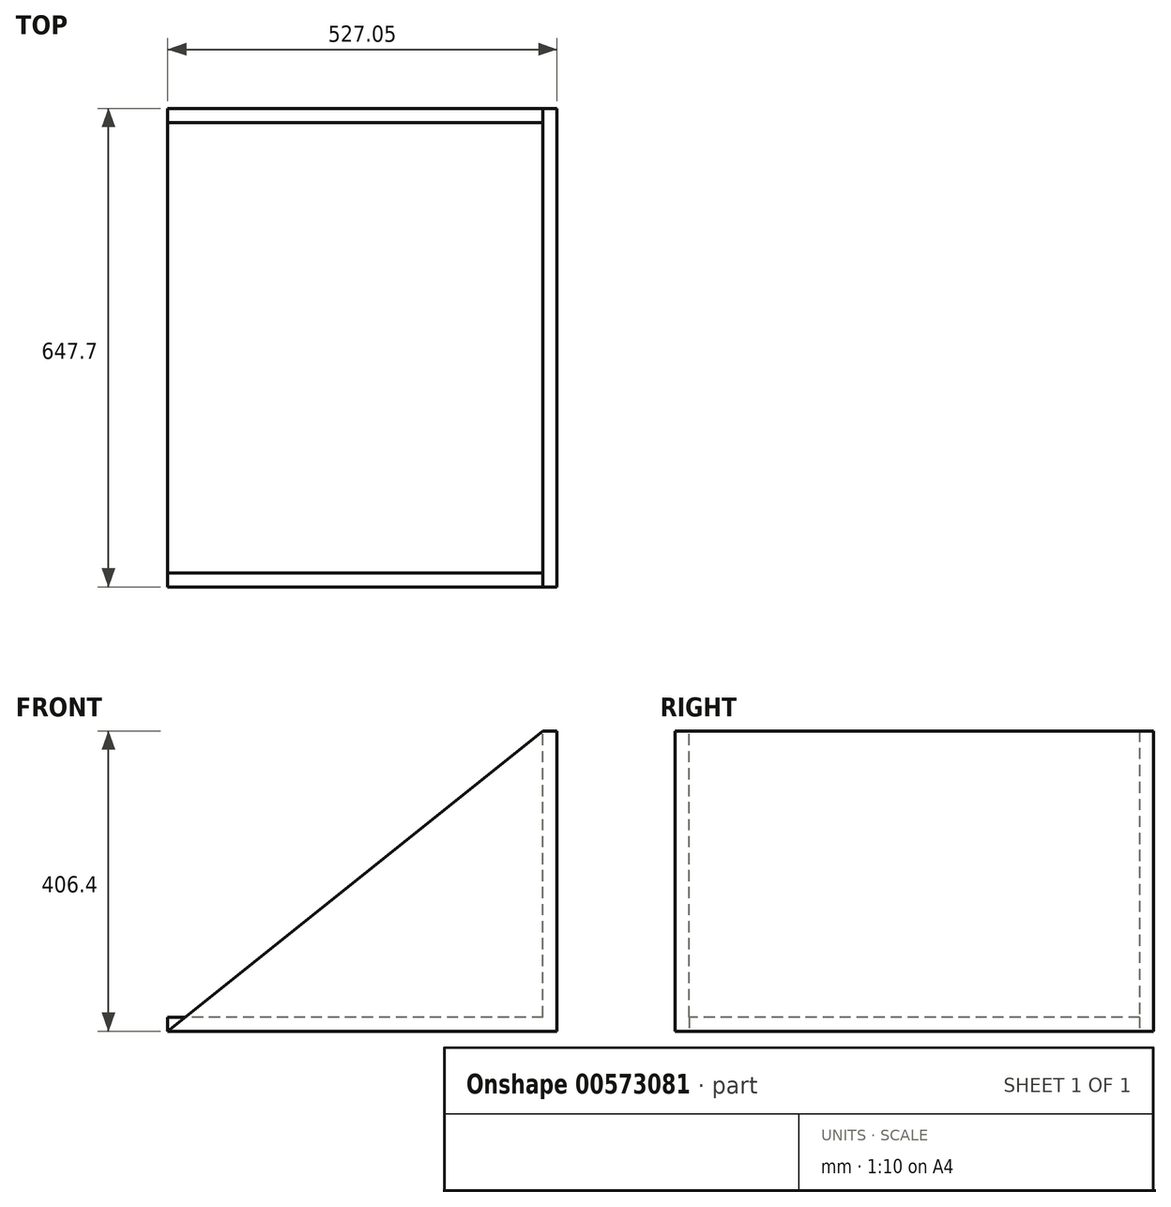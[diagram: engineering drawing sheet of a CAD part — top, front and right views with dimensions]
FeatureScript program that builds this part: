
annotation { "Feature Type Name" : "Feature", "Feature Type Description" : "" }
export const myFeature = defineFeature(function(context is Context, id is Id, definition is map)
    precondition{}
    {
        {
            var Q0;
            Q0=qCreatedBy(makeId("Top.planeOp"),FACE);
            var sketch = newSketch(context, id + "F0", { "sketchPlane" : qUnion([Q0])});
            skLineSegment(sketch, "E0.bottom", {"start": v(254, 304.8) * mm, "end": v(-254, 304.8) * mm});
            skLineSegment(sketch, "E0.top", {"start": v(254, -304.8) * mm, "end": v(-254, -304.8) * mm});
            skLineSegment(sketch, "E0.left", {"start": v(254, 304.8) * mm, "end": v(254, -304.8) * mm});
            skLineSegment(sketch, "E0.right", {"start": v(-254, 304.8) * mm, "end": v(-254, -304.8) * mm});
            skPoint(sketch, "E0.middle", {"position": v(0, 0) * mm});
            skSolve(sketch);
        }
        {
            var Q0;
            Q0=makeQuery(id+"F0.imprint","IMPRINT",FACE,{"disambiguationData":[TD([[makeQuery(id+"F0.imprint","IMPRINT",EDGE,{"derivedFrom":sQuery(id+"F0.wireOp",EDGE,"E0.bottom")}),1.0]])]});
            extrude(context, id + "F1", {"entities" : qUnion([Q0]), "depth" : 19.05 * mm, "offsetDistance" : 25.4 * mm});
        }
        {
            var Q0;
            Q0=makeQuery(id+"F1.opExtrude","SWEPT_FACE",FACE,{"disambiguationData":[OSD([sQuery(id+"F0.wireOp",EDGE,"E0.top")])]});
            var sketch = newSketch(context, id + "F2", { "sketchPlane" : qUnion([Q0])});
            skLineSegment(sketch, "E1.bottom", {"start": v(254, 0) * mm, "end": v(-254, 0) * mm});
            skLineSegment(sketch, "E1.left", {"start": v(254, 0) * mm, "end": v(254, 406.4) * mm});
            skLineSegment(sketch, "E2", {"start": v(254, 406.4) * mm, "end": v(-254, 0) * mm});
            skSolve(sketch);
        }
        {
            var Q0;
            {var subQ0=sQuery(id+"F2.wireOp",EDGE,"E1.left");var subQ3=sQuery(id+"F2.wireOp",EDGE,"E2");var subQ4=makeQuery(id+"F2.imprint","INTERSECT",VERTEX,{"derivedFrom":[subQ0,subQ3]});Q0=makeQuery(id+"F2.imprint","IMPRINT",FACE,{"disambiguationData":[TD([[makeQuery(id+"F2.imprint","IMPRINT",EDGE,{"disambiguationData":[TD([[subQ4,1.0]])],"derivedFrom":subQ0}),1.0]])]});}
            var Q1;
            {var subQ0=sQuery(id+"F2.wireOp",EDGE,"E1.bottom");Q1=makeQuery(id+"F2.imprint","IMPRINT",FACE,{"disambiguationData":[TD([[makeQuery(id+"F2.imprint","IMPRINT",EDGE,{"derivedFrom":subQ0}),-1.0]])]});}
            extrude(context, id + "F3", {"entities" : qUnion([Q0, Q1]), "operationType" : NewBodyOperationType.ADD, "depth" : 19.05 * mm, "offsetDistance" : 25.4 * mm});
        }
        {
            var Q0;
            Q0=makeQuery(id+"F1.opExtrude","SWEPT_FACE",FACE,{"disambiguationData":[OSD([sQuery(id+"F0.wireOp",EDGE,"E0.bottom")])]});
            var sketch = newSketch(context, id + "F4", { "sketchPlane" : qUnion([Q0])});
            skLineSegment(sketch, "E3.0.0", {"start": v(-254, 0) * mm, "end": v(-254, 406.4) * mm});
            skLineSegment(sketch, "E3.0.1", {"start": v(-254, 406.4) * mm, "end": v(254, 0) * mm});
            skLineSegment(sketch, "E3.0.2", {"start": v(254, 0) * mm, "end": v(-254, 0) * mm});
            skSolve(sketch);
        }
        {
            var Q0;
            {var subQ0=sQuery(id+"F4.wireOp",EDGE,"E3.0.0");var subQ3=sQuery(id+"F4.wireOp",EDGE,"E3.0.1");var subQ4=makeQuery(id+"F4.imprint","INTERSECT",VERTEX,{"derivedFrom":[subQ0,subQ3]});Q0=makeQuery(id+"F4.imprint","IMPRINT",FACE,{"disambiguationData":[TD([[makeQuery(id+"F4.imprint","IMPRINT",EDGE,{"disambiguationData":[TD([[subQ4,1.0]])],"derivedFrom":subQ0}),-1.0]])]});}
            var Q1;
            {var subQ0=sQuery(id+"F4.wireOp",EDGE,"E3.0.2");Q1=makeQuery(id+"F4.imprint","IMPRINT",FACE,{"disambiguationData":[TD([[makeQuery(id+"F4.imprint","IMPRINT",EDGE,{"derivedFrom":subQ0}),1.0]])]});}
            extrude(context, id + "F5", {"entities" : qUnion([Q0, Q1]), "operationType" : NewBodyOperationType.ADD, "depth" : 19.05 * mm, "offsetDistance" : 25.4 * mm});
        }
        {
            var Q0;
            Q0=makeQuery(id+"F5.boolean.opBoolean","MERGE",FACE,{"derivedFrom":[makeQuery(id+"F3.boolean.opBoolean","MERGE",FACE,{"derivedFrom":[makeQuery(id+"F1.opExtrude","SWEPT_FACE",FACE,{"disambiguationData":[OSD([sQuery(id+"F0.wireOp",EDGE,"E0.left")])]}),makeQuery(id+"F3.opExtrude","SWEPT_FACE",FACE,{"disambiguationData":[OSD([sQuery(id+"F2.wireOp",EDGE,"E1.left")])]})]}),makeQuery(id+"F5.opExtrude","SWEPT_FACE",FACE,{"disambiguationData":[OSD([sQuery(id+"F4.wireOp",EDGE,"E3.0.0")])]})]});
            var sketch = newSketch(context, id + "F6", { "sketchPlane" : qUnion([Q0])});
            skLineSegment(sketch, "E4.bottom", {"start": v(323.85, 0) * mm, "end": v(-323.85, 0) * mm});
            skLineSegment(sketch, "E4.top", {"start": v(323.85, 406.4) * mm, "end": v(-323.85, 406.4) * mm});
            skLineSegment(sketch, "E4.left", {"start": v(323.85, 0) * mm, "end": v(323.85, 406.4) * mm});
            skLineSegment(sketch, "E4.right", {"start": v(-323.85, 0) * mm, "end": v(-323.85, 406.4) * mm});
            skSolve(sketch);
        }
        {
            var Q0;
            Q0=makeQuery(id+"F6.imprint","IMPRINT",FACE,{"disambiguationData":[TD([[makeQuery(id+"F6.imprint","IMPRINT",EDGE,{"derivedFrom":makeQuery(id+"F1.opExtrude","CAP_EDGE",EDGE,{"disambiguationData":[OSD([sQuery(id+"F0.wireOp",EDGE,"E0.left")])],"isStart":false})}),-1.0]])]});
            var Q1;
            Q1=makeQuery(id+"F6.imprint","IMPRINT",FACE,{"disambiguationData":[TD([[makeQuery(id+"F6.imprint","IMPRINT",EDGE,{"derivedFrom":sQuery(id+"F6.wireOp",EDGE,"E4.bottom")}),-1.0]])]});
            extrude(context, id + "F7", {"entities" : qUnion([Q0, Q1]), "operationType" : NewBodyOperationType.ADD, "depth" : 19.05 * mm, "offsetDistance" : 25.4 * mm});
        }
    });
